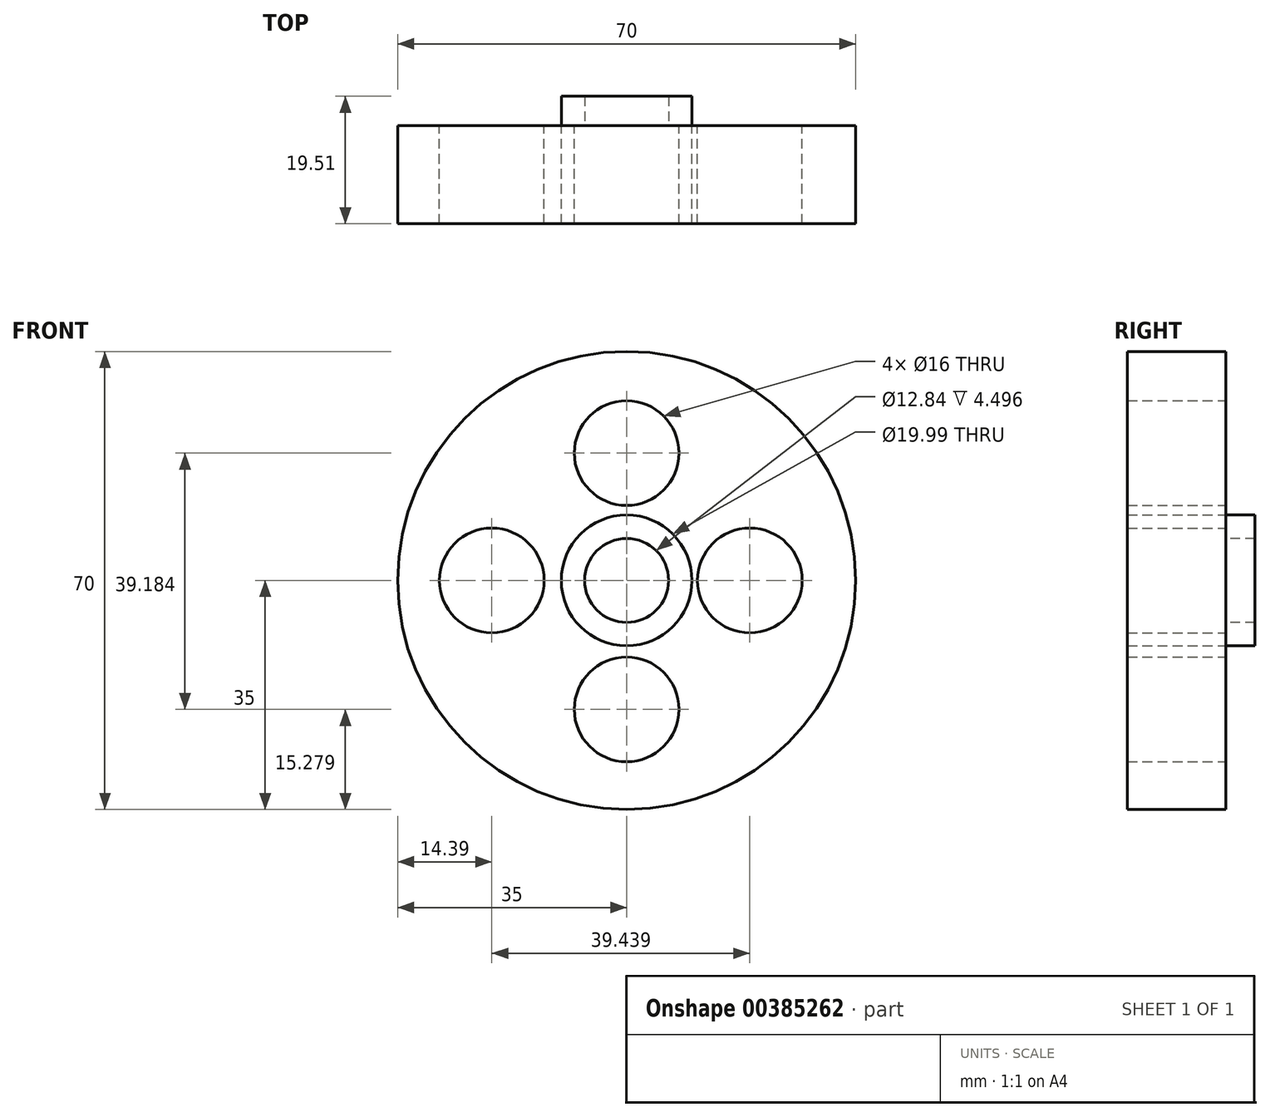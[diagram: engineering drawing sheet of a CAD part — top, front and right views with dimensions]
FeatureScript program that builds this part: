
annotation { "Feature Type Name" : "Feature", "Feature Type Description" : "" }
export const myFeature = defineFeature(function(context is Context, id is Id, definition is map)
    precondition{}
    {
        {
            var Q0;
            Q0=qCreatedBy(makeId("Front.planeOp"),FACE);
            var sketch = newSketch(context, id + "F0", { "sketchPlane" : qUnion([Q0])});
            skCircle(sketch, "E0", {"center": v(0, 0) * mm, "radius": 35 * mm});
            skCircle(sketch, "E1", {"center": v(0, 0) * mm, "radius": 30 * mm});
            skCircle(sketch, "E2", {"center": v(0, 0) * mm, "radius": 10 * mm});
            skCircle(sketch, "E3", {"center": v(0, 19.46) * mm, "radius": 8 * mm});
            skCircle(sketch, "E4", {"center": v(18.83, 0) * mm, "radius": 8 * mm});
            skCircle(sketch, "E5", {"center": v(0, -19.72) * mm, "radius": 8 * mm});
            skCircle(sketch, "E6", {"center": v(-20.6, 0) * mm, "radius": 8 * mm});
            skCircle(sketch, "E7", {"center": v(0, 0) * mm, "radius": 6.42 * mm});
            skSolve(sketch);
        }
        {
            var Q0;
            Q0 = qSketchRegion(id + "F0", true);
            var Q1;
            Q1=makeQuery(id+"F0.imprint","IMPRINT",FACE,{"disambiguationData":[TD([[makeQuery(id+"F0.imprint","IMPRINT",EDGE,{"derivedFrom":sQuery(id+"F0.wireOp",EDGE,"E1")}),1.0]])]});
            extrude(context, id + "F1", {"entities" : qUnion([Q0, Q1]), "depth" : 15 * mm});
        }
        {
            var Q0;
            Q0=makeQuery(id+"F0.imprint","IMPRINT",FACE,{"disambiguationData":[TD([[makeQuery(id+"F0.imprint","IMPRINT",EDGE,{"derivedFrom":sQuery(id+"F0.wireOp",EDGE,"E2")}),1.0]])]});
            extrude(context, id + "F2", {"entities" : qUnion([Q0]), "oppositeDirection" : true, "depth" : 4.5 * mm});
        }
    });
